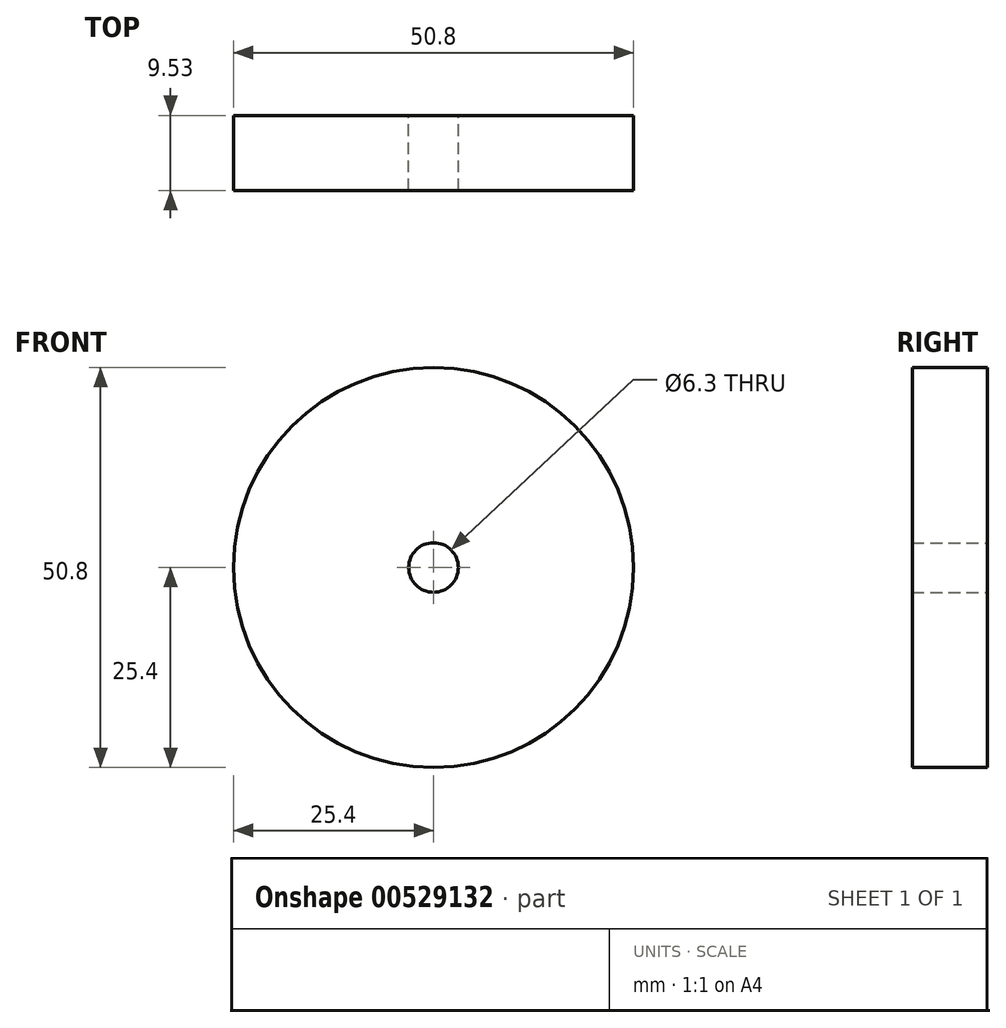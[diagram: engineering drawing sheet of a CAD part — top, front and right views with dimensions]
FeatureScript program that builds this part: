
annotation { "Feature Type Name" : "Feature", "Feature Type Description" : "" }
export const myFeature = defineFeature(function(context is Context, id is Id, definition is map)
    precondition{}
    {
        {
            var Q0;
            Q0=qCreatedBy(makeId("Front.planeOp"),FACE);
            var sketch = newSketch(context, id + "F0", { "sketchPlane" : qUnion([Q0])});
            skCircle(sketch, "E0", {"center": v(0, 0) * mm, "radius": 25.4 * mm});
            skCircle(sketch, "E1", {"center": v(0, 0) * mm, "radius": 3.15 * mm});
            skSolve(sketch);
        }
        {
            var Q0;
            Q0 = qSketchRegion(id + "F0", true);
            extrude(context, id + "F1", {"entities" : qUnion([Q0]), "depth" : 9.52 * mm, "offsetDistance" : 25.4 * mm});
        }
    });
